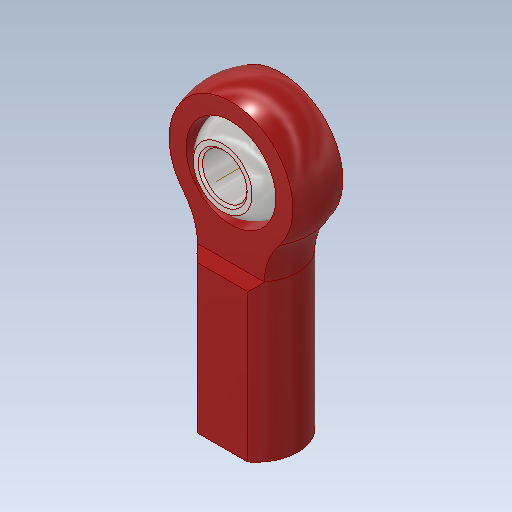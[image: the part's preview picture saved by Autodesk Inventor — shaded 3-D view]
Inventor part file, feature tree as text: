
AUTODESK INVENTOR PART (.ipt)
format: ipt  version: 2020 (Build 240168000, 168)  size: 602,624 bytes
history: native  units: in
note: dims shown in document units (in); Inventor stores cm internally (conversion verified against a paired STEP export)
features: other x4, plane x1
ambient origin geometry x8: Origin, YZ Plane, XZ Plane, XY Plane, X Axis, Y Axis, Z Axis, Center Point
bodies: Solid1 (feature_tree), Solid2 (feature_tree)
feature tree (5):
  plane  "Work Plane1"
  other  "Work Axis1"
  other  "Work Point1"
  parser-record x1  (decoder bookkeeping rows leaked as tree rows — omitted from the tree; the rows remain in map.json)
  other  "NONE:1"
